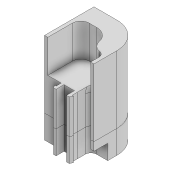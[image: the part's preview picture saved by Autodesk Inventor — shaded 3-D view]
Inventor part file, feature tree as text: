
AUTODESK INVENTOR PART (.ipt)
format: ipt  version: 2021 (Build 250183000, 183)  size: 212,992 bytes
history: native  units: mm
features: other x6, extrude x1, direct_edit x1, sketch x1, move_body x1
ambient origin geometry x8: Origin, YZ Plane, XZ Plane, XY Plane, X Axis, Y Axis, Z Axis, Center Point
bodies: Volumenkörper1 (feature_tree), Volumenkörper2 (feature_tree)
feature tree (10):
  other  "Corner1.ipt"
  other  "Buttom2.ipt"
  extrude  "Extrusion1"  Depth=10.0mm
  direct_edit  "Direktbearbeitung1"
  other  "Volumenkörper1::Corner1.ipt"
  other  "Bezeichnung1"
  sketch  "Skizze1"  dims[d0=10.0mm d1=8.5mm d2=0.0mm d3=0.0mm d4=10.0mm d5=-1.5mm d6=0.0mm d7=0.0mm]
  other  "Volumenkörper1::Buttom2.ipt"
  other  "Bezeichnung2"
  move_body  "Verschieben1"
